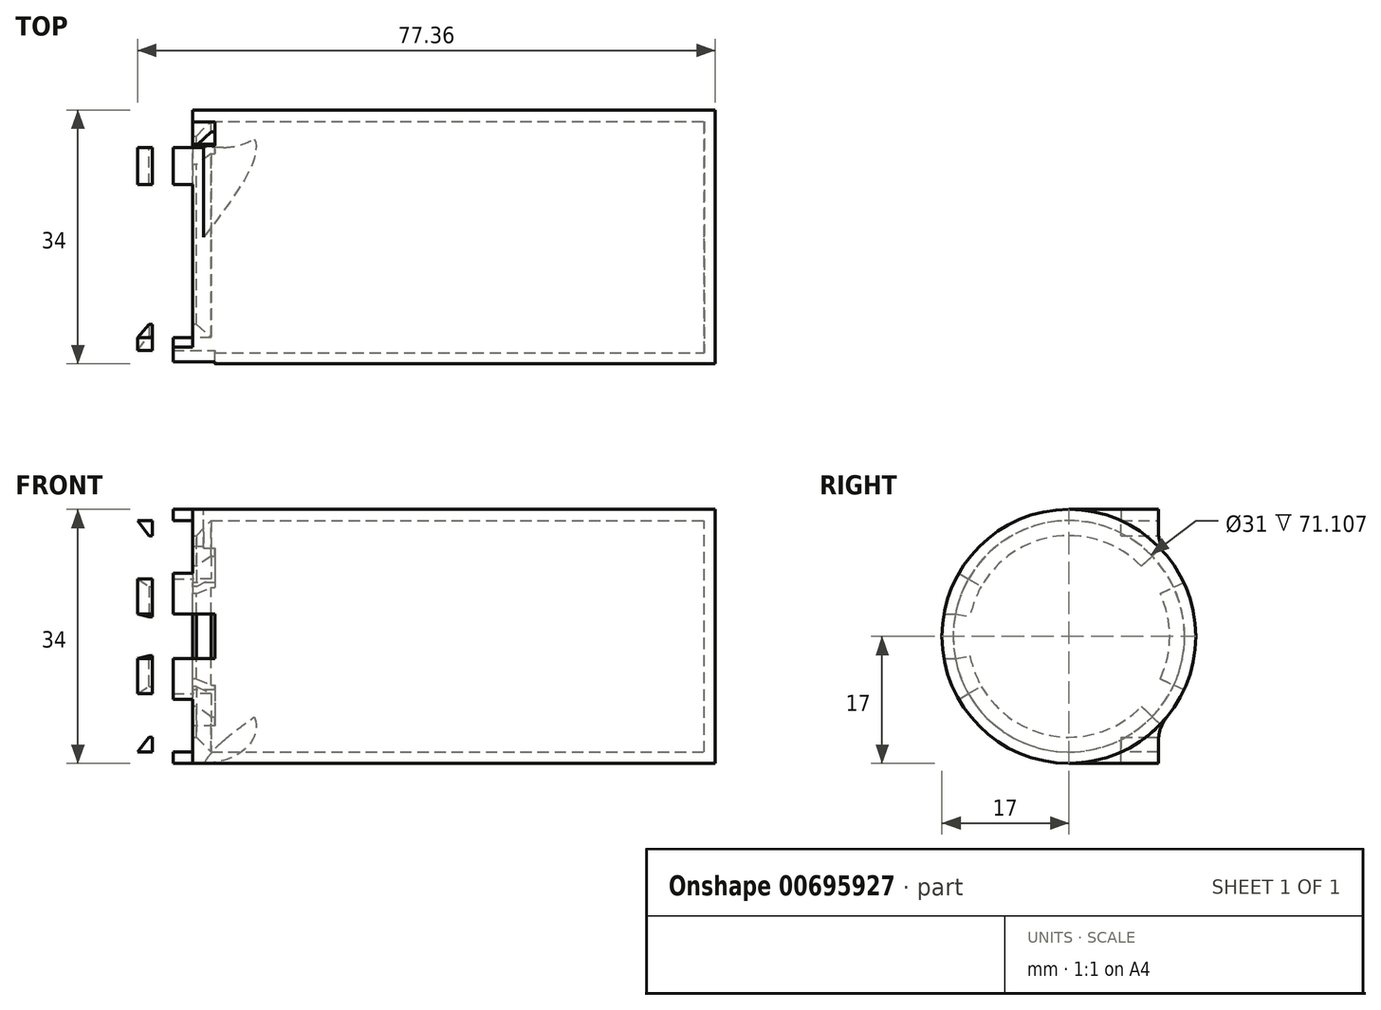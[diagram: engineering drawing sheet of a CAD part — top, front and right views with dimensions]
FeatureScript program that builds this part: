
annotation { "Feature Type Name" : "Feature", "Feature Type Description" : "" }
export const myFeature = defineFeature(function(context is Context, id is Id, definition is map)
    precondition{}
    {
        {
            var Q0;
            Q0=qCreatedBy(makeId("Right.planeOp"),FACE);
            var sketch = newSketch(context, id + "F0", { "sketchPlane" : qUnion([Q0])});
            skArc(sketch, "E0", {"start": v(0, 17) * mm, "mid": v(-17, 0) * mm, "end": v(0, -17) * mm});
            skLineSegment(sketch, "E1", {"start": v(0, 17) * mm, "end": v(12, 17) * mm});
            skLineSegment(sketch, "E2", {"start": v(12, -17) * mm, "end": v(0, -17) * mm});
            skCircle(sketch, "E3", {"center": v(0, 0) * mm, "radius": 15.5 * mm});
            skArc(sketch, "E4", {"start": v(12, -12.04) * mm, "mid": v(17, 0) * mm, "end": v(12, 12.04) * mm});
            skLineSegment(sketch, "E5", {"start": v(12, -17) * mm, "end": v(12, -12.04) * mm});
            skLineSegment(sketch, "E6", {"start": v(12, 12.04) * mm, "end": v(12, 17) * mm});
            skSolve(sketch);
        }
        {
            var Q0;
            Q0=qCreatedBy(makeId("Right.planeOp"),FACE);
            var sketch = newSketch(context, id + "F1", { "sketchPlane" : qUnion([Q0])});
            skCircle(sketch, "E7", {"center": v(0, 0) * mm, "radius": 17 * mm});
            skCircle(sketch, "E8", {"center": v(0, 0) * mm, "radius": 15.5 * mm});
            skSolve(sketch);
        }
        {
            var Q0;
            Q0 = qSketchRegion(id + "F0", true);
            extrude(context, id + "F2", {"entities" : qUnion([Q0]), "oppositeDirection" : true, "depth" : 1.5 * mm, "offsetDistance" : 25 * mm});
        }
        {
            var Q0;
            Q0=makeQuery(id+"F1.imprint","IMPRINT",FACE,{"disambiguationData":[TD([[makeQuery(id+"F1.imprint","IMPRINT",EDGE,{"derivedFrom":sQuery(id+"F1.wireOp",EDGE,"E7")}),1.0]])]});
            extrude(context, id + "F3", {"entities" : qUnion([Q0]), "operationType" : NewBodyOperationType.ADD, "depth" : 67 * mm, "offsetDistance" : 25 * mm});
        }
        {
            var Q0;
            Q0=makeQuery(id+"F3.opExtrude","CAP_EDGE",EDGE,{"disambiguationData":[OSD([sQuery(id+"F1.wireOp",EDGE,"E7")])],"isStart":true});
            fillet(context, id + "F4", {"entities" : qUnion([Q0]), "radius" : 7 * mm, "tangentPropagation" : true, "allowEdgeOverflow" : false});
        }
        {
            var Q0;
            Q0=makeQuery(id+"F3.opExtrude","CAP_FACE",FACE,{"disambiguationData":[OSD([sQuery(id+"F1.wireOp",EDGE,"E7"),sQuery(id+"F1.wireOp",EDGE,"E8")])],"isStart":false});
            var sketch = newSketch(context, id + "F5", { "sketchPlane" : qUnion([Q0])});
            skCircle(sketch, "E9", {"center": v(0, 0) * mm, "radius": 17 * mm});
            skSolve(sketch);
        }
        {
            var Q0;
            Q0 = qSketchRegion(id + "F5", true);
            extrude(context, id + "F6", {"entities" : qUnion([Q0]), "operationType" : NewBodyOperationType.ADD, "depth" : 1.5 * mm, "offsetDistance" : 25 * mm});
        }
        {
            var Q0;
            Q0=qCreatedBy(makeId("Top.planeOp"),FACE);
            var sketch = newSketch(context, id + "F7", { "sketchPlane" : qUnion([Q0])});
            skLineSegment(sketch, "E10", {"start": v(-1.5, -15.5) * mm, "end": v(1, -15.5) * mm});
            skLineSegment(sketch, "E11", {"start": v(-1.5, -13.5) * mm, "end": v(-1.5, -15.5) * mm});
            skLineSegment(sketch, "E12", {"start": v(1, -15.5) * mm, "end": v(-1, -13.5) * mm});
            skLineSegment(sketch, "E13", {"start": v(-1, -13.5) * mm, "end": v(-1.5, -13.5) * mm});
            skSolve(sketch);
        }
        {
            var Q0;
            Q0 = qSketchRegion(id + "F7", true);
            var Q1;
            Q1=makeQuery(id+"F3.boolean.opBoolean","MERGE",FACE,{"derivedFrom":[makeQuery(id+"F2.opExtrude","SWEPT_FACE",FACE,{"disambiguationData":[OSD([sQuery(id+"F0.wireOp",EDGE,"E3")])]}),makeQuery(id+"F3.opExtrude","SWEPT_FACE",FACE,{"disambiguationData":[OSD([sQuery(id+"F1.wireOp",EDGE,"E8")])]})]});
            revolve(context, id + "F8", {"operationType" : NewBodyOperationType.ADD, "surfaceOperationType" : NewSurfaceOperationType.NEW, "entities" : qUnion([Q0]), "axis" : qUnion([Q1]), "revolveType" : RevolveType.FULL});
        }
        {
            var Q0;
            Q0=makeQuery(id+"F8.boolean.opBoolean","MERGE",FACE,{"derivedFrom":[makeQuery(id+"F2.opExtrude","CAP_FACE",FACE,{"disambiguationData":[OSD([sQuery(id+"F0.wireOp",EDGE,"E0"),sQuery(id+"F0.wireOp",EDGE,"E1"),sQuery(id+"F0.wireOp",EDGE,"IBGzmEdN-dqS2-86vs-1kzg-eUyeRONaIWmC"),sQuery(id+"F0.wireOp",EDGE,"E2"),sQuery(id+"F0.wireOp",EDGE,"E3")])],"isStart":false}),makeQuery(id+"F8.opRevolve","SWEPT_FACE",FACE,{"disambiguationData":[OSD([sQuery(id+"F7.wireOp",EDGE,"E11")])]})]});
            var sketch = newSketch(context, id + "F9", { "sketchPlane" : qUnion([Q0])});
            skLineSegment(sketch, "E14.bottom", {"start": v(-12, -17) * mm, "end": v(-7, -17) * mm});
            skLineSegment(sketch, "E14.top", {"start": v(-12, -15.5) * mm, "end": v(-7, -15.5) * mm});
            skLineSegment(sketch, "E14.left", {"start": v(-12, -17) * mm, "end": v(-12, -15.5) * mm});
            skLineSegment(sketch, "E14.right", {"start": v(-7, -17) * mm, "end": v(-7, -15.5) * mm});
            skLineSegment(sketch, "E15", {"start": v(0, 0) * mm, "end": v(-17, 0) * mm, "construction": true});
            skLineSegment(sketch, "E16.MirrorCS", {"start": v(-12, 17) * mm, "end": v(-12, 15.5) * mm});
            skLineSegment(sketch, "E17.MirrorCS", {"start": v(-7, 17) * mm, "end": v(-7, 15.5) * mm});
            skLineSegment(sketch, "E18.MirrorCS", {"start": v(-12, 15.5) * mm, "end": v(-7, 15.5) * mm});
            skLineSegment(sketch, "E19.MirrorCS", {"start": v(-12, 17) * mm, "end": v(-7, 17) * mm});
            skSolve(sketch);
        }
        {
            var Q0;
            Q0 = qSketchRegion(id + "F9", true);
            extrude(context, id + "F10", {"entities" : qUnion([Q0]), "operationType" : NewBodyOperationType.ADD, "depth" : 3 / 406.4 * mm + 2.6 * mm, "offsetDistance" : 25 * mm});
        }
        {
            var Q0;
            Q0=makeQuery(id+"F8.boolean.opBoolean","MERGE",FACE,{"derivedFrom":[makeQuery(id+"F2.opExtrude","CAP_FACE",FACE,{"disambiguationData":[OSD([sQuery(id+"F0.wireOp",EDGE,"E0"),sQuery(id+"F0.wireOp",EDGE,"E1"),sQuery(id+"F0.wireOp",EDGE,"IBGzmEdN-dqS2-86vs-1kzg-eUyeRONaIWmC"),sQuery(id+"F0.wireOp",EDGE,"E2"),sQuery(id+"F0.wireOp",EDGE,"E3")])],"isStart":false}),makeQuery(id+"F8.opRevolve","SWEPT_FACE",FACE,{"disambiguationData":[OSD([sQuery(id+"F7.wireOp",EDGE,"E11")])]})]});
            var sketch = newSketch(context, id + "F11", { "sketchPlane" : qUnion([Q0])});
            skArc(sketch, "E20", {"start": v(16.82, -2.5) * mm, "mid": v(17, 0) * mm, "end": v(16.82, 2.5) * mm, "construction": true});
            skArc(sketch, "E21", {"start": v(15.32, -2.5) * mm, "mid": v(15.52, 0) * mm, "end": v(15.32, 2.5) * mm, "construction": true});
            skLineSegment(sketch, "E22", {"start": v(16.82, 2.5) * mm, "end": v(15.32, 2.5) * mm, "construction": true});
            skLineSegment(sketch, "E23", {"start": v(16.82, -2.5) * mm, "end": v(15.32, -2.5) * mm, "construction": true});
            skLineSegment(sketch, "E24", {"start": v(15.32, 2.5) * mm, "end": v(15.32, -2.5) * mm, "construction": true});
            skLineSegment(sketch, "E25", {"start": v(17, 0) * mm, "end": v(0, 0) * mm, "construction": true});
            skArc(sketch, "E26", {"start": v(14.76, -8.43) * mm, "mid": v(15.98, -5.8) * mm, "end": v(16.73, -3) * mm});
            skArc(sketch, "E27", {"start": v(13.46, -7.69) * mm, "mid": v(14.52, -5.41) * mm, "end": v(15.2, -3) * mm});
            skLineSegment(sketch, "E28", {"start": v(16.73, -3) * mm, "end": v(15.2, -3) * mm});
            skLineSegment(sketch, "E29", {"start": v(14.76, -8.43) * mm, "end": v(13.46, -7.69) * mm});
            skLineSegment(sketch, "E30", {"start": v(0, 0) * mm, "end": v(14.76, -8.43) * mm, "construction": true});
            skLineSegment(sketch, "E31", {"start": v(13.46, -7.69) * mm, "end": v(15.2, -3) * mm, "construction": true});
            skLineSegment(sketch, "E32.MirrorCS", {"start": v(16.73, 3) * mm, "end": v(15.2, 3) * mm});
            skLineSegment(sketch, "E33.MirrorCS", {"start": v(14.76, 8.43) * mm, "end": v(13.46, 7.69) * mm});
            skArc(sketch, "E34.MirrorCS", {"start": v(13.46, 7.69) * mm, "mid": v(14.52, 5.41) * mm, "end": v(15.2, 3) * mm});
            skArc(sketch, "E35.MirrorCS", {"start": v(14.76, 8.43) * mm, "mid": v(15.98, 5.8) * mm, "end": v(16.73, 3) * mm});
            skSolve(sketch);
        }
        {
            var Q0;
            Q0 = qSketchRegion(id + "F11", true);
            extrude(context, id + "F12", {"entities" : qUnion([Q0]), "operationType" : NewBodyOperationType.ADD, "depth" : 3 / 406.4 * mm + 2.6 * mm, "offsetDistance" : 25 * mm});
        }
        {
            var Q0;
            Q0=makeQuery(id+"F10.boolean.opBoolean","MERGE",FACE,{"derivedFrom":[makeQuery(id+"F2.opExtrude","SWEPT_FACE",FACE,{"disambiguationData":[OSD([sQuery(id+"F0.wireOp",EDGE,"IBGzmEdN-dqS2-86vs-1kzg-eUyeRONaIWmC")])]}),makeQuery(id+"F10.opExtrude","SWEPT_FACE",FACE,{"disambiguationData":[OSD([sQuery(id+"F9.wireOp",EDGE,"E14.left")])]}),makeQuery(id+"F10.opExtrude","SWEPT_FACE",FACE,{"disambiguationData":[OSD([sQuery(id+"F9.wireOp",EDGE,"E16.MirrorCS")])]})]});
            var sketch = newSketch(context, id + "F13", { "sketchPlane" : qUnion([Q0])});
            skLineSegment(sketch, "E36", {"start": v(6.86, 13.5) * mm, "end": v(6.86, 15.5) * mm});
            skLineSegment(sketch, "E37", {"start": v(6.86, 15.5) * mm, "end": v(8.86, 15.5) * mm});
            skLineSegment(sketch, "E38", {"start": v(0, 0) * mm, "end": v(6.44, 0) * mm, "construction": true});
            skLineSegment(sketch, "E39", {"start": v(8.86, 15.5) * mm, "end": v(7.36, 13.5) * mm});
            skLineSegment(sketch, "E40", {"start": v(7.36, 13.5) * mm, "end": v(6.86, 13.5) * mm});
            skLineSegment(sketch, "E41.MirrorCS", {"start": v(7.36, -13.5) * mm, "end": v(6.86, -13.5) * mm});
            skLineSegment(sketch, "E42.MirrorCS", {"start": v(8.86, -15.5) * mm, "end": v(7.36, -13.5) * mm});
            skLineSegment(sketch, "E43.MirrorCS", {"start": v(6.86, -15.5) * mm, "end": v(8.86, -15.5) * mm});
            skLineSegment(sketch, "E44.MirrorCS", {"start": v(6.86, -13.5) * mm, "end": v(6.86, -15.5) * mm});
            skSolve(sketch);
        }
        {
            var Q0;
            Q0 = qSketchRegion(id + "F13", true);
            var Q1;
            Q1=makeQuery(id+"F10.opExtrude","SWEPT_FACE",FACE,{"disambiguationData":[OSD([sQuery(id+"F9.wireOp",EDGE,"E17.MirrorCS")])]});
            extrude(context, id + "F14", {"entities" : qUnion([Q0]), "operationType" : NewBodyOperationType.ADD, "endBound" : BoundingType.UP_TO_SURFACE, "oppositeDirection" : true, "depth" : 25 * mm, "endBoundEntityFace" : qUnion([Q1]), "offsetDistance" : 25 * mm});
        }
        {
            var Q0;
            Q0=makeQuery(id+"F12.opExtrude","SWEPT_FACE",FACE,{"disambiguationData":[OSD([sQuery(id+"F11.wireOp",EDGE,"E33.MirrorCS")])]});
            var sketch = newSketch(context, id + "F15", { "sketchPlane" : qUnion([Q0])});
            skLineSegment(sketch, "E45", {"start": v(-8.86, -15.5) * mm, "end": v(-6.86, -15.5) * mm});
            skLineSegment(sketch, "E46", {"start": v(-6.86, -15.5) * mm, "end": v(-6.86, -13.5) * mm});
            skLineSegment(sketch, "E47", {"start": v(-8.86, -15.5) * mm, "end": v(-7.36, -13.5) * mm});
            skLineSegment(sketch, "E48", {"start": v(-7.36, -13.5) * mm, "end": v(-6.86, -13.5) * mm});
            skSolve(sketch);
        }
        {
            var Q0;
            Q0=makeQuery(id+"F15.imprint","IMPRINT",FACE,{"disambiguationData":[TD([[makeQuery(id+"F15.imprint","IMPRINT",EDGE,{"derivedFrom":sQuery(id+"F15.wireOp",EDGE,"E45")}),1.0]])]});
            var Q1;
            Q1=makeQuery(id+"F12.opExtrude","CAP_EDGE",EDGE,{"disambiguationData":[OSD([sQuery(id+"F11.wireOp",EDGE,"E34.MirrorCS")])],"isStart":false});
            sweep(context, id + "F16", {"operationType" : NewBodyOperationType.ADD, "profiles" : qUnion([Q0]), "path" : qUnion([Q1])});
        }
        {
            var Q0;
            Q0=makeQuery(id+"F12.opExtrude","SWEPT_FACE",FACE,{"disambiguationData":[OSD([sQuery(id+"F11.wireOp",EDGE,"E29")])]});
            var sketch = newSketch(context, id + "F17", { "sketchPlane" : qUnion([Q0])});
            skLineSegment(sketch, "E49", {"start": v(-8.86, 15.5) * mm, "end": v(-6.86, 15.5) * mm});
            skLineSegment(sketch, "E50", {"start": v(-6.86, 15.5) * mm, "end": v(-6.86, 13.5) * mm});
            skLineSegment(sketch, "E51", {"start": v(-8.86, 15.5) * mm, "end": v(-7.36, 13.5) * mm});
            skLineSegment(sketch, "E52", {"start": v(-7.36, 13.5) * mm, "end": v(-6.86, 13.5) * mm});
            skSolve(sketch);
        }
        {
            var Q0;
            Q0=makeQuery(id+"F17.imprint","IMPRINT",FACE,{"disambiguationData":[TD([[makeQuery(id+"F17.imprint","IMPRINT",EDGE,{"derivedFrom":sQuery(id+"F17.wireOp",EDGE,"E49")}),-1.0]])]});
            var Q1;
            Q1=makeQuery(id+"F12.opExtrude","CAP_EDGE",EDGE,{"disambiguationData":[OSD([sQuery(id+"F11.wireOp",EDGE,"E27")])],"isStart":false});
            sweep(context, id + "F18", {"operationType" : NewBodyOperationType.ADD, "profiles" : qUnion([Q0]), "path" : qUnion([Q1])});
        }
        {
            var Q0;
            Q0=makeQuery(id+"F8.boolean.opBoolean","MERGE",FACE,{"derivedFrom":[makeQuery(id+"F2.opExtrude","CAP_FACE",FACE,{"disambiguationData":[OSD([sQuery(id+"F0.wireOp",EDGE,"E0"),sQuery(id+"F0.wireOp",EDGE,"E1"),sQuery(id+"F0.wireOp",EDGE,"IBGzmEdN-dqS2-86vs-1kzg-eUyeRONaIWmC"),sQuery(id+"F0.wireOp",EDGE,"E2"),sQuery(id+"F0.wireOp",EDGE,"E3")])],"isStart":false}),makeQuery(id+"F8.opRevolve","SWEPT_FACE",FACE,{"disambiguationData":[OSD([sQuery(id+"F7.wireOp",EDGE,"E11")])]})]});
            var sketch = newSketch(context, id + "F19", { "sketchPlane" : qUnion([Q0])});
            skArc(sketch, "E53", {"start": v(16.73, 3) * mm, "mid": v(17, 0) * mm, "end": v(16.73, -3) * mm});
            skArc(sketch, "E54", {"start": v(11.72, -6.7) * mm, "mid": v(13.5, 0) * mm, "end": v(11.72, 6.7) * mm});
            skLineSegment(sketch, "E55", {"start": v(16.73, 3) * mm, "end": v(15.2, 3) * mm});
            skLineSegment(sketch, "E56", {"start": v(16.73, -3) * mm, "end": v(15.2, -3) * mm});
            skArc(sketch, "E57", {"start": v(15.2, 3) * mm, "mid": v(14.52, 5.41) * mm, "end": v(13.46, 7.69) * mm});
            skArc(sketch, "E58", {"start": v(13.46, -7.69) * mm, "mid": v(14.52, -5.41) * mm, "end": v(15.2, -3) * mm});
            skLineSegment(sketch, "E59", {"start": v(13.46, -7.69) * mm, "end": v(11.72, -6.7) * mm});
            skLineSegment(sketch, "E60", {"start": v(13.46, 7.69) * mm, "end": v(11.72, 6.7) * mm});
            skSolve(sketch);
        }
        {
            var Q0;
            Q0 = qSketchRegion(id + "F19", true);
            extrude(context, id + "F20", {"entities" : qUnion([Q0]), "operationType" : NewBodyOperationType.REMOVE, "oppositeDirection" : true, "depth" : 3 * mm, "offsetDistance" : 25 * mm});
        }
        {
            var Q0;
            Q0=makeQuery(id+"F2.opExtrude","SWEPT_EDGE",EDGE,{"disambiguationData":[OSD([sQuery(id+"F0.wireOp",EDGE,"E4"),sQuery(id+"F0.wireOp",EDGE,"E6")])]});
            var Q1;
            Q1=makeQuery(id+"F2.opExtrude","SWEPT_EDGE",EDGE,{"disambiguationData":[OSD([sQuery(id+"F0.wireOp",EDGE,"E4"),sQuery(id+"F0.wireOp",EDGE,"E5")])]});
            fillet(context, id + "F21", {"entities" : qUnion([Q0, Q1]), "radius" : 5 * mm, "tangentPropagation" : true, "allowEdgeOverflow" : false});
        }
        {
            var Q0;
            Q0=makeQuery(id+"F8.boolean.opBoolean","MERGE",FACE,{"derivedFrom":[makeQuery(id+"F2.opExtrude","CAP_FACE",FACE,{"disambiguationData":[OSD([sQuery(id+"F0.wireOp",EDGE,"E0"),sQuery(id+"F0.wireOp",EDGE,"E1"),sQuery(id+"F0.wireOp",EDGE,"E2"),sQuery(id+"F0.wireOp",EDGE,"E3"),sQuery(id+"F0.wireOp",EDGE,"E4"),sQuery(id+"F0.wireOp",EDGE,"E5"),sQuery(id+"F0.wireOp",EDGE,"E6")])],"isStart":false}),makeQuery(id+"F8.opRevolve","SWEPT_FACE",FACE,{"disambiguationData":[OSD([sQuery(id+"F7.wireOp",EDGE,"E11")])]})]});
            var sketch = newSketch(context, id + "F22", { "sketchPlane" : qUnion([Q0])});
            skLineSegment(sketch, "E61", {"start": v(-15.4, -7.18) * mm, "end": v(-12.24, -5.7) * mm});
            skLineSegment(sketch, "E62", {"start": v(-12.24, -5.7) * mm, "end": v(-9.71, -9.38) * mm});
            skLineSegment(sketch, "E63", {"start": v(-9.71, -9.38) * mm, "end": v(-12.4, -11.98) * mm});
            skArc(sketch, "E64", {"start": v(-15.4, -7.18) * mm, "mid": v(-17.3, -11.7) * mm, "end": v(-12.4, -11.98) * mm});
            skLineSegment(sketch, "E65", {"start": v(-12.4, -11.98) * mm, "end": v(0, 0) * mm, "construction": true});
            skLineSegment(sketch, "E66", {"start": v(0, 0) * mm, "end": v(-15.4, -7.18) * mm, "construction": true});
            skLineSegment(sketch, "E67", {"start": v(0, 0) * mm, "end": v(-17, 0) * mm, "construction": true});
            skArc(sketch, "E68.MirrorCS", {"start": v(-15.4, 7.18) * mm, "mid": v(-17.3, 11.7) * mm, "end": v(-12.4, 11.98) * mm});
            skLineSegment(sketch, "E69.MirrorCS", {"start": v(-15.4, 7.18) * mm, "end": v(-12.24, 5.7) * mm});
            skLineSegment(sketch, "E70.MirrorCS", {"start": v(-9.71, 9.38) * mm, "end": v(-12.4, 11.98) * mm});
            skLineSegment(sketch, "E71.MirrorCS", {"start": v(-12.24, 5.7) * mm, "end": v(-9.71, 9.38) * mm});
            skSolve(sketch);
        }
        {
            var Q0;
            Q0 = qSketchRegion(id + "F22", true);
            extrude(context, id + "F23", {"entities" : qUnion([Q0]), "operationType" : NewBodyOperationType.REMOVE, "oppositeDirection" : true, "depth" : 3 * mm, "offsetDistance" : 25 * mm});
        }
    });
